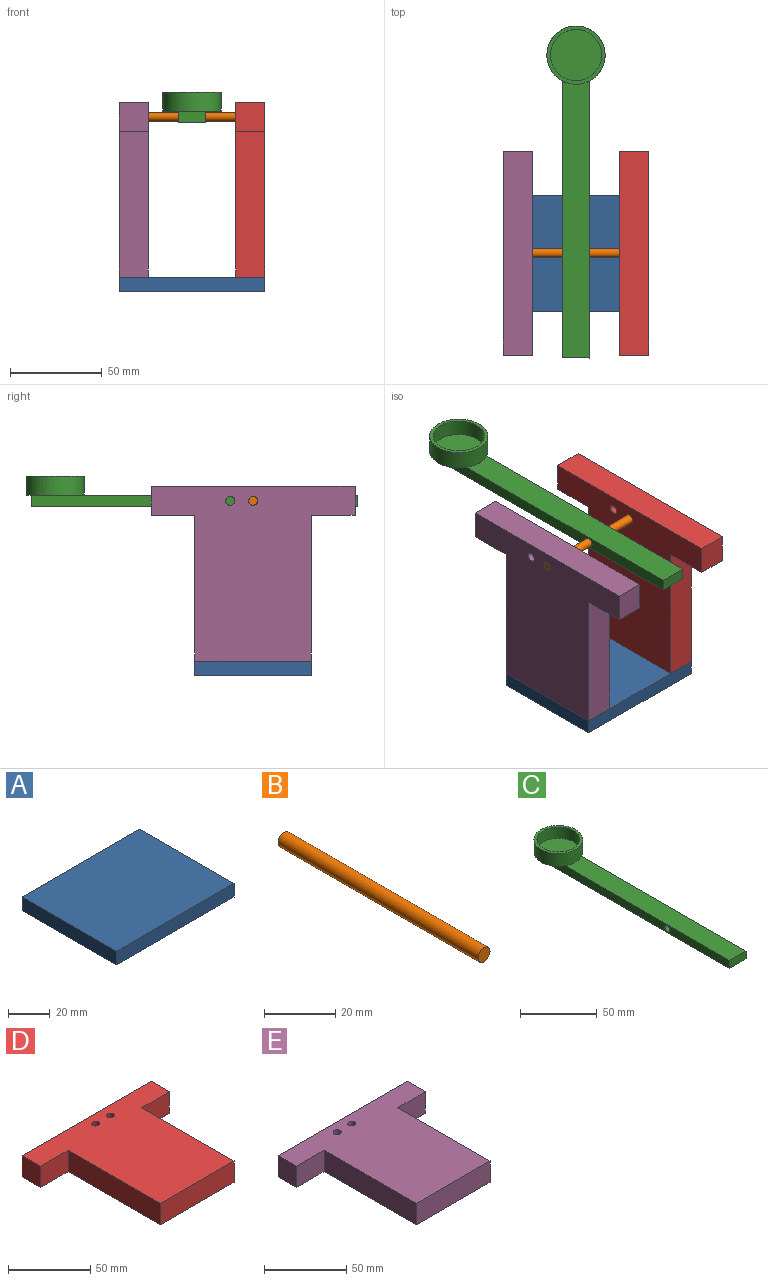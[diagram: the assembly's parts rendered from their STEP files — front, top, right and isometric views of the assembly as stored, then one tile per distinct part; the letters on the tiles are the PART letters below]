
ASSEMBLY  parts=5 mates=4
PART A: 6 faces, bbox 79.4x63.5x7.9 mm
  f0: plane 63.5x7.94mm, normal (-1,0,0), area 504mm2, adj f1,f3,f4,f5
  f1: plane 79.38x7.94mm, normal (0,-1,0), area 630mm2, adj f0,f2,f4,f5
  f2: plane 63.5x7.94mm, normal (1,0,0), area 504mm2, adj f1,f3,f4,f5
  f3: plane 79.38x7.94mm, normal (0,1,0), area 630mm2, adj f0,f2,f4,f5
  f4: plane 79.38x63.5mm, normal (0,0,1), area 5040.3mm2, adj f0,f1,f2,f3
  f5: plane 79.38x63.5mm, normal (0,0,-1), area 5040.3mm2, adj f0,f1,f2,f3
PART B: 3 faces, bbox 4.8x79.4x4.8 mm
  f0: cylinder r=2.38mm len=79.38mm, axis (0,1,0), area 1187.6mm2, adj f1,f2
  f1: plane 4.76x4.76mm, normal (0,-1,0), area 17.8mm2, adj f0
  f2: plane 4.76x4.76mm, normal (0,1,0), area 17.8mm2, adj f0
PART C: 12 faces, bbox 31.8x181x16.5 mm
  f0: plane 177.8x6.35mm, normal (-1,0,0), area 1111.1mm2, adj f1,f3,f4,f5,f6,f9
  f1: plane 177.8x15.24mm, normal (0,0,-1), area 2709.7mm2, adj f0,f2,f4,f5
  f2: plane 177.8x6.35mm, normal (1,0,0), area 1111.1mm2, adj f1,f3,f4,f5,f6,f9
  f3: plane 151.17x15.24mm, normal (0,0,1), area 2283.8mm2, adj f0,f2,f4,f7
  f4: plane 15.24x6.35mm, normal (0,-1,0), area 96.8mm2, adj f0,f1,f2,f3
  f5: plane 15.24x6.35mm, normal (0,1,0), area 96.8mm2, adj f0,f1,f2,f9
  f6: cylinder r=2.39mm len=15.24mm, axis (1,0,0), area 228.6mm2, adj f0,f2
  f7: cylinder r=15.88mm len=31.75mm, axis (0,0,-1), area 1013.4mm2, adj f3,f8,f9
  f8: plane 31.75x31.75mm, normal (0,0,1), area 178.6mm2, adj f7,f10
  f9: plane 31.75x29.8mm, normal (0,0,-1), area 365.9mm2, adj f0,f2,f5,f7
  f10: cylinder r=13.97mm len=27.94mm, axis (0,0,1), area 780.3mm2, adj f8,f11
  f11: plane 27.94x27.94mm, normal (0,0,1), area 613.1mm2, adj f10
PART D: 12 faces, bbox 111.1x95.3x15.9 mm
  f0: plane 79.38x15.88mm, normal (-1,0,0), area 1260.1mm2, adj f1,f7,f8,f9
  f1: plane 63.5x15.88mm, normal (0,-1,0), area 1008.1mm2, adj f0,f2,f8,f9
  f2: plane 79.38x15.88mm, normal (1,0,0), area 1260.1mm2, adj f1,f3,f8,f9
  f3: plane 23.81x15.88mm, normal (0,-1,0), area 378mm2, adj f2,f4,f8,f9
  f4: plane 15.88x15.88mm, normal (1,0,0), area 252mm2, adj f3,f5,f8,f9
  f5: plane 111.13x15.88mm, normal (0,1,0), area 1764.1mm2, adj f4,f6,f8,f9
  f6: plane 15.88x15.88mm, normal (-1,0,0), area 252mm2, adj f5,f7,f8,f9
  f7: plane 23.81x15.88mm, normal (0,-1,0), area 378mm2, adj f0,f6,f8,f9
  f8: plane 111.13x95.25mm, normal (0,0,1), area 6768.2mm2, adj f0,f1,f2,f3,f4,f5,f6,f7
  f9: plane 111.13x95.25mm, normal (0,0,-1), area 6768.2mm2, adj f0,f1,f2,f3,f4,f5,f6,f7
  f10: cylinder r=2.4mm len=15.88mm, axis (0,0,1), area 239.4mm2, adj f8,f9
  f11: cylinder r=2.4mm len=15.88mm, axis (0,0,1), area 239.4mm2, adj f8,f9
PART E: 12 faces, bbox 111.1x95.2x15.9 mm
  f0: plane 79.38x15.88mm, normal (-1,0,0), area 1260.1mm2, adj f1,f7,f8,f9
  f1: plane 63.5x15.88mm, normal (0,-1,0), area 1008.1mm2, adj f0,f2,f8,f9
  f2: plane 79.38x15.88mm, normal (1,0,0), area 1260.1mm2, adj f1,f3,f8,f9
  f3: plane 23.81x15.88mm, normal (0,-1,0), area 378mm2, adj f2,f4,f8,f9
  f4: plane 15.88x15.81mm, normal (1,0,0), area 250.9mm2, adj f3,f5,f8,f9
  f5: plane 111.13x15.88mm, normal (0,1,0), area 1764.1mm2, adj f4,f6,f8,f9
  f6: plane 15.88x15.81mm, normal (-1,0,0), area 250.9mm2, adj f5,f7,f8,f9
  f7: plane 23.81x15.88mm, normal (0,-1,0), area 378mm2, adj f0,f6,f8,f9
  f8: plane 111.13x95.18mm, normal (0,0,1), area 6760.7mm2, adj f0,f1,f2,f3,f4,f5,f6,f7
  f9: plane 111.13x95.18mm, normal (0,0,-1), area 6760.7mm2, adj f0,f1,f2,f3,f4,f5,f6,f7
  f10: cylinder r=2.4mm len=15.88mm, axis (0,0,1), area 239.4mm2, adj f8,f9
  f11: cylinder r=2.4mm len=15.88mm, axis (0,0,1), area 239.4mm2, adj f8,f9
PLACE A t=(-0.19,-17.18,-7.11)mm
PLACE B rot(axis=(0,0,-1),90deg) t=(48.01,-5.61,88.14)mm
PLACE C rot(axis=(0.82,0.26,-0.51),0deg) t=(6.67,115.04,91.05)mm
PLACE D rot(axis=(0.58,0.58,0.58),120deg) t=(32.13,-3.54,47.66)mm
PLACE E rot(axis=(0.58,-0.58,-0.58),120deg) t=(-15.49,-7.39,23.01)mm
MATE fastened D.f1 <-> A.f4  axis (0,0,-1) through (48.01,-5.61,0.82)mm
MATE fastened E.f1 <-> A.f4  axis (0,0,-1) through (-31.37,-5.61,0.82)mm
MATE revolute B.f0 <-> D.f11  axis (1,0,0) through (48.01,-5.61,88.14)mm
MATE fastened C.f6 <-> B.f0  axis (1,0,0) through (8.32,-5.61,88.14)mm
